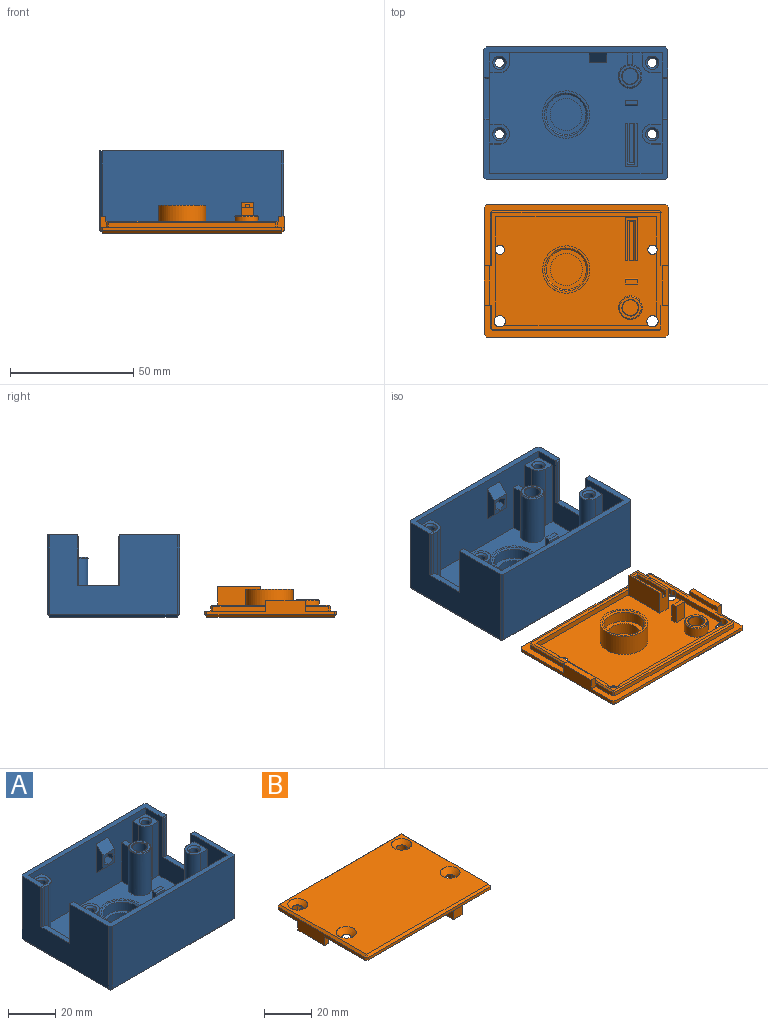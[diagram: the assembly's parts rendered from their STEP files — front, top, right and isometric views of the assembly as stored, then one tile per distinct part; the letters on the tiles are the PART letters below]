
ASSEMBLY  parts=2 mates=1
PART A: 120 faces, bbox 74.8x53.8x33.4 mm
  f0: plane 49x31mm, normal (-1,0,0), area 634.4mm2, adj f3,f4,f17,f19,f21,f23,f42,f43
  f1: plane 51.8x32.4mm, normal (1,0,0), area 1199.7mm2, adj f17,f21,f23,f81,f82,f83,f84,f85
  f2: plane 7x7mm, normal (0,-1,0), area 27.3mm2, adj f66,f67,f68,f69,f70,f71,f72,f73
  f3: plane 70x49mm, normal (0,0,1), area 2721.3mm2, adj f0,f4,f5,f16,f19,f25,f33,f34
  f4: plane 70x31mm, normal (0,-1,0), area 1569mm2, adj f0,f3,f16,f17,f33,f34,f35,f38
  f5: cylinder r=4.8mm len=21.6mm, axis (0,0,-1), area 602.9mm2, adj f3,f33,f34,f35,f113
  f6: plane 51.8x32.4mm, normal (-1,0,0), area 1325.7mm2, adj f17,f21,f22,f90,f94,f96,f103,f106
  f7: plane 72.8x32.4mm, normal (0,-1,0), area 2358.7mm2, adj f21,f87,f93,f96
  f8: cylinder r=1.9mm len=29.6mm, axis (0,0,1), area 353.4mm2, adj f13,f110
  f9: cylinder r=1.9mm len=29.6mm, axis (0,0,1), area 353.4mm2, adj f13,f111
  f10: cylinder r=1.9mm len=29.6mm, axis (0,0,1), area 353.4mm2, adj f13,f112
  f11: plane 72.8x32.4mm, normal (0,1,0), area 2358.7mm2, adj f17,f85,f89,f90
  f12: cylinder r=1.9mm len=29.6mm, axis (0,0,1), area 353.4mm2, adj f13,f109
  f13: plane 72.8x51.8mm, normal (0,0,-1), area 3725.7mm2, adj f8,f9,f10,f12,f88,f89,f93,f94
  f14: plane 19.9x1.2mm, normal (0,-1,0), area 23.9mm2, adj f23,f97,f98,f99
  f15: plane 19.9x1.2mm, normal (0,-1,0), area 23.9mm2, adj f22,f106,f107,f108
  f16: plane 49x31mm, normal (1,0,0), area 718.4mm2, adj f3,f4,f17,f19,f21,f22,f36,f39
  f17: plane 74.8x12.3mm, normal (0,0,1), area 226mm2, adj f0,f1,f4,f6,f11,f16,f85,f90
  f18: plane 19.9x1.2mm, normal (0,1,0), area 23.9mm2, adj f23,f100,f101,f102
  f19: plane 70x31mm, normal (0,1,0), area 2170mm2, adj f0,f3,f16,f21
  f20: plane 19.9x1.2mm, normal (0,1,0), area 23.9mm2, adj f22,f103,f104,f105
  f21: plane 74.8x24.3mm, normal (0,0,1), area 283.6mm2, adj f0,f1,f6,f7,f16,f19,f87,f96
  f22: plane 17.2x2.4mm, normal (0,0,1), area 39.1mm2, adj f6,f15,f16,f20,f103,f104,f106,f107
  f23: plane 17.2x2.4mm, normal (0,0,1), area 39.1mm2, adj f0,f1,f14,f18,f97,f98,f100,f101
  f24: cylinder r=8.15mm len=16.3mm, axis (0,0,-1), area 225.3mm2, adj f29,f115
  f25: cylinder r=9.6mm len=19.2mm, axis (0,0,-1), area 542.9mm2, adj f3,f26
  f26: plane 19.2x19.2mm, normal (0,0,1), area 49mm2, adj f25,f115
  f27: plane 13x13mm, normal (0,0,1), area 132.7mm2, adj f28
  f28: cylinder r=6.5mm len=13mm, axis (0,0,-1), area 204.2mm2, adj f27,f29
  f29: plane 16.3x16.3mm, normal (0,0,1), area 75.9mm2, adj f24,f28
  f30: cylinder r=3.2mm len=21.8mm, axis (0,0,-1), area 438.3mm2, adj f32,f114
  f31: plane 8.8x8.8mm, normal (0,0,1), area 24.5mm2, adj f113,f114
  f32: plane 6.4x6.4mm, normal (0,0,1), area 32.2mm2, adj f30
  f33: plane 20x4.85mm, normal (1,0,0), area 97mm2, adj f3,f4,f5,f35
  f34: plane 20x4.85mm, normal (-1,0,0), area 97mm2, adj f3,f4,f5,f35
  f35: plane 4.85x2.4mm, normal (0,0,1), area 11.4mm2, adj f4,f5,f33,f34
  f36: plane 28x4mm, normal (0,-1,0), area 112mm2, adj f3,f16,f37,f39
  f37: cylinder r=4mm len=28mm, axis (0,0,-1), area 175.9mm2, adj f3,f36,f38,f39
  f38: plane 28x4mm, normal (1,0,0), area 112mm2, adj f3,f4,f37,f39
  f39: plane 8x8mm, normal (0,0,1), area 37.7mm2, adj f4,f16,f36,f37,f38,f112
  f40: plane 28x4mm, normal (-1,0,0), area 112mm2, adj f3,f4,f41,f43
  f41: cylinder r=4mm len=28mm, axis (0,0,-1), area 175.9mm2, adj f3,f40,f42,f43
  f42: plane 28x4mm, normal (0,-1,0), area 112mm2, adj f0,f3,f41,f43
  f43: plane 8x8mm, normal (0,0,1), area 37.7mm2, adj f0,f4,f40,f41,f42,f111
  f44: plane 28x4mm, normal (0,1,0), area 112mm2, adj f3,f16,f46,f47
  f45: plane 28x4mm, normal (0,-1,0), area 112mm2, adj f3,f16,f46,f47
  f46: cylinder r=4mm len=28mm, axis (0,0,-1), area 351.9mm2, adj f3,f44,f45,f47
  f47: plane 8x8mm, normal (0,0,1), area 34.2mm2, adj f16,f44,f45,f46,f110
  f48: plane 28x4mm, normal (0,1,0), area 112mm2, adj f0,f3,f49,f51
  f49: cylinder r=4mm len=28mm, axis (0,0,-1), area 351.9mm2, adj f3,f48,f50,f51
  f50: plane 28x4mm, normal (0,-1,0), area 112mm2, adj f0,f3,f49,f51
  f51: plane 8x8mm, normal (0,0,1), area 34.2mm2, adj f0,f48,f49,f50,f109
  f52: plane 7x5mm, normal (0,1,0), area 29.2mm2, adj f3,f53,f54,f56,f57,f59,f60,f116
  f53: plane 16x1.8mm, normal (0,0,1), area 28.8mm2, adj f52,f54,f55,f56
  f54: plane 16x2.4mm, normal (1,0,0), area 38.4mm2, adj f52,f53,f55,f116
  f55: plane 2.4x1.8mm, normal (0,1,0), area 4.3mm2, adj f53,f54,f56,f118
  f56: plane 16x2.4mm, normal (-1,0,0), area 38.4mm2, adj f52,f53,f55,f117
  f57: plane 17.6x7mm, normal (-1,0,0), area 123.2mm2, adj f3,f52,f58,f60
  f58: plane 7x5mm, normal (0,-1,0), area 35mm2, adj f3,f57,f59,f60
  f59: plane 17.6x7mm, normal (1,0,0), area 123.2mm2, adj f3,f52,f58,f60
  f60: plane 17.6x5mm, normal (0,0,1), area 38.2mm2, adj f52,f57,f58,f59,f116,f117,f118
  f61: plane 5x2.4mm, normal (-1,0,0), area 11.8mm2, adj f3,f62,f64,f65,f119
  f62: plane 5x4.4mm, normal (0,-1,0), area 22mm2, adj f3,f61,f63,f119
  f63: plane 5x2.4mm, normal (1,0,0), area 11.8mm2, adj f3,f62,f64,f65,f119
  f64: plane 5x5mm, normal (0,1,0), area 25mm2, adj f3,f61,f63,f65
  f65: plane 5x1.8mm, normal (0,0,1), area 9mm2, adj f61,f63,f64,f119
  f66: plane 15x4mm, normal (1,0,0), area 44mm2, adj f2,f4,f68,f69
  f67: plane 15x4mm, normal (-1,0,0), area 44mm2, adj f2,f4,f68,f69
  f68: plane 7x4mm, normal (0,-0.71,0.71), area 39.6mm2, adj f2,f4,f66,f67
  f69: plane 7x4mm, normal (0,-0.71,-0.71), area 39.6mm2, adj f2,f4,f66,f67
  f70: plane 4x2.5mm, normal (0.5,0,0.87), area 11.5mm2, adj f2,f71,f75,f76
  f71: plane 4x2.5mm, normal (-0.5,0,0.87), area 11.5mm2, adj f2,f70,f72,f76
  f72: plane 4x2.89mm, normal (-1,0,0), area 11.5mm2, adj f2,f71,f73,f76
  f73: plane 4x2.5mm, normal (-0.5,0,-0.87), area 11.5mm2, adj f2,f72,f74,f76
  f74: plane 4x2.5mm, normal (0.5,0,-0.87), area 11.5mm2, adj f2,f73,f75,f76
  f75: plane 4x2.89mm, normal (1,0,0), area 11.5mm2, adj f2,f70,f74,f76
  f76: plane 5.77x5mm, normal (0,-1,0), area 21.7mm2, adj f70,f71,f72,f73,f74,f75
  f77: plane 7x1.4mm, normal (0,0,-1), area 9.8mm2, adj f0,f78,f80,f84
  f78: plane 12x1.4mm, normal (0,1,0), area 16.8mm2, adj f0,f77,f79,f83
  f79: plane 7x1.4mm, normal (0,0,1), area 9.8mm2, adj f0,f78,f80,f81
  f80: plane 12x1.4mm, normal (0,-1,0), area 16.8mm2, adj f0,f77,f79,f82
  f81: plane 9x1mm, normal (0.71,0,0.71), area 11.3mm2, adj f1,f79,f82,f83
  f82: plane 14x1mm, normal (0.71,-0.71,0), area 18.4mm2, adj f1,f80,f81,f84
  f83: plane 14x1mm, normal (0.71,0.71,0), area 18.4mm2, adj f1,f78,f81,f84
  f84: plane 9x1mm, normal (0.71,0,-0.71), area 11.3mm2, adj f1,f77,f82,f83
  f85: plane 32.4x1mm, normal (0.71,0.71,0), area 45.8mm2, adj f1,f11,f17,f86
  f86: plane 1x1mm, normal (0.58,0.58,-0.58), area 0.9mm2, adj f85,f88,f89
  f87: plane 32.4x1mm, normal (0.71,-0.71,0), area 45.8mm2, adj f1,f7,f21,f91
  f88: plane 51.8x1mm, normal (0.71,0,-0.71), area 73.3mm2, adj f1,f13,f86,f91
  f89: plane 72.8x1mm, normal (0,0.71,-0.71), area 103mm2, adj f11,f13,f86,f92
  f90: plane 32.4x1mm, normal (-0.71,0.71,0), area 45.8mm2, adj f6,f11,f17,f92
  f91: plane 1x1mm, normal (0.58,-0.58,-0.58), area 0.9mm2, adj f87,f88,f93
  f92: plane 1x1mm, normal (-0.58,0.58,-0.58), area 0.9mm2, adj f89,f90,f94
  f93: plane 72.8x1mm, normal (0,-0.71,-0.71), area 103mm2, adj f7,f13,f91,f95
  f94: plane 51.8x1mm, normal (-0.71,0,-0.71), area 73.3mm2, adj f6,f13,f92,f95
  f95: plane 1x1mm, normal (-0.58,-0.58,-0.58), area 0.9mm2, adj f93,f94,f96
  f96: plane 32.4x1mm, normal (-0.71,-0.71,0), area 45.8mm2, adj f6,f7,f21,f95
  f97: plane 20.5x0.6mm, normal (0.71,-0.71,0), area 17.1mm2, adj f1,f14,f23,f99
  f98: plane 20.5x0.6mm, normal (-0.71,-0.71,0), area 17.1mm2, adj f0,f14,f23,f99
  f99: plane 2.4x0.6mm, normal (0,-0.71,0.71), area 1.5mm2, adj f14,f17,f97,f98
  f100: plane 20.5x0.6mm, normal (0.71,0.71,0), area 17.1mm2, adj f1,f18,f23,f102
  f101: plane 20.5x0.6mm, normal (-0.71,0.71,0), area 17.1mm2, adj f0,f18,f23,f102
  f102: plane 2.4x0.6mm, normal (0,0.71,0.71), area 1.5mm2, adj f18,f21,f100,f101
  f103: plane 20.5x0.6mm, normal (-0.71,0.71,0), area 17.1mm2, adj f6,f20,f22,f105
  f104: plane 20.5x0.6mm, normal (0.71,0.71,0), area 17.1mm2, adj f16,f20,f22,f105
  f105: plane 2.4x0.6mm, normal (0,0.71,0.71), area 1.5mm2, adj f20,f21,f103,f104
  f106: plane 20.5x0.6mm, normal (-0.71,-0.71,0), area 17.1mm2, adj f6,f15,f22,f108
  f107: plane 20.5x0.6mm, normal (0.71,-0.71,0), area 17.1mm2, adj f15,f16,f22,f108
  f108: plane 2.4x0.6mm, normal (0,-0.71,0.71), area 1.5mm2, adj f15,f17,f106,f107
  f109: cone r=1.9mm half-angle=45deg, axis (0,0,1), area 16.3mm2, adj f12,f51
  f110: cone r=1.9mm half-angle=45deg, axis (0,0,1), area 16.3mm2, adj f8,f47
  f111: cone r=1.9mm half-angle=45deg, axis (0,0,1), area 16.3mm2, adj f9,f43
  f112: cone r=1.9mm half-angle=45deg, axis (0,0,1), area 16.3mm2, adj f10,f39
  f113: cone r=4.4mm half-angle=45deg, axis (0,0,-1), area 16.3mm2, adj f5,f31
  f114: cone r=3mm half-angle=45deg, axis (0,0,1), area 5.9mm2, adj f30,f31
  f115: cone r=8.15mm half-angle=45deg, axis (0,0,1), area 45.1mm2, adj f24,f26
  f116: plane 16.6x0.6mm, normal (0.71,0,0.71), area 13.8mm2, adj f52,f54,f60,f118
  f117: plane 16.6x0.6mm, normal (-0.71,0,0.71), area 13.8mm2, adj f52,f56,f60,f118
  f118: plane 3x0.6mm, normal (0,0.71,0.71), area 2mm2, adj f55,f60,f116,f117
  f119: plane 5x0.6mm, normal (0,-0.71,0.71), area 4.2mm2, adj f61,f62,f63,f65
PART B: 90 faces, bbox 74.8x53.8x12.4 mm
  f0: plane 65.2x44.2mm, normal (0,0,-1), area 2371.2mm2, adj f6,f7,f8,f9,f13,f19,f22,f24
  f1: plane 74.8x12.9mm, normal (0,0,-1), area 247.7mm2, adj f3,f4,f10,f36,f40,f48,f51,f52
  f2: plane 74.8x24.9mm, normal (0,0,-1), area 310.1mm2, adj f4,f5,f10,f38,f41,f49,f50,f59
  f3: plane 72.8x1.4mm, normal (0,1,0), area 101.9mm2, adj f1,f61,f65,f66
  f4: plane 51.8x5.9mm, normal (-1,0,0), area 144.5mm2, adj f1,f2,f40,f41,f43,f61,f63,f64
  f5: plane 72.8x1.4mm, normal (0,-1,0), area 101.9mm2, adj f2,f63,f69,f72
  f6: cylinder r=1.9mm len=3.8mm, axis (0,0,-1), area 6.4mm2, adj f0,f45,f57,f58,f60
  f7: cylinder r=2.3mm len=4.6mm, axis (0,0,-1), area 24.7mm2, adj f0,f47,f53,f58,f60
  f8: cylinder r=1.9mm len=3.8mm, axis (0,0,-1), area 6.4mm2, adj f0,f44,f54,f55,f60
  f9: cylinder r=2.3mm len=4.6mm, axis (0,0,-1), area 24.7mm2, adj f0,f46,f53,f54,f60
  f10: plane 51.8x5.9mm, normal (1,0,0), area 144.5mm2, adj f1,f2,f36,f38,f39,f66,f70,f72
  f11: plane 72.8x51.8mm, normal (0,0,1), area 3549.4mm2, adj f44,f45,f46,f47,f64,f65,f69,f70
  f12: cylinder r=8.15mm len=16.3mm, axis (0,0,1), area 225.3mm2, adj f17,f79
  f13: cylinder r=9.6mm len=19.2mm, axis (0,0,1), area 542.9mm2, adj f0,f14
  f14: plane 19.2x19.2mm, normal (0,0,-1), area 49mm2, adj f13,f79
  f15: plane 13x13mm, normal (0,0,-1), area 132.7mm2, adj f16
  f16: cylinder r=6.5mm len=13mm, axis (0,0,1), area 204.2mm2, adj f15,f17
  f17: plane 16.3x16.3mm, normal (0,0,-1), area 75.9mm2, adj f12,f16
  f18: cylinder r=3.2mm len=6.4mm, axis (0,0,1), area 88.5mm2, adj f21,f74
  f19: cylinder r=4.8mm len=9.6mm, axis (0,0,1), area 126.7mm2, adj f0,f73
  f20: plane 8.8x8.8mm, normal (0,0,-1), area 24.5mm2, adj f73,f74
  f21: plane 6.4x6.4mm, normal (0,0,-1), area 32.2mm2, adj f18
  f22: plane 10x5mm, normal (0,1,0), area 43.9mm2, adj f0,f23,f29,f31,f32,f34,f35,f81
  f23: plane 16x1.8mm, normal (0,0,-1), area 28.8mm2, adj f22,f29,f30,f31
  f24: plane 8x2.4mm, normal (-1,0,0), area 19mm2, adj f0,f25,f27,f28,f80
  f25: plane 7.4x5mm, normal (0,-1,0), area 37mm2, adj f0,f24,f26,f80
  f26: plane 8x2.4mm, normal (1,0,0), area 19mm2, adj f0,f25,f27,f28,f80
  f27: plane 8x5mm, normal (0,1,0), area 40mm2, adj f0,f24,f26,f28
  f28: plane 5x1.8mm, normal (0,0,-1), area 9mm2, adj f24,f26,f27,f80
  f29: plane 16x2.6mm, normal (1,0,0), area 41.6mm2, adj f22,f23,f30,f81
  f30: plane 2.6x1.8mm, normal (0,1,0), area 4.7mm2, adj f23,f29,f31,f83
  f31: plane 16x2.6mm, normal (-1,0,0), area 41.6mm2, adj f22,f23,f30,f82
  f32: plane 17.6x10mm, normal (-1,0,0), area 176mm2, adj f0,f22,f33,f35
  f33: plane 10x5mm, normal (0,-1,0), area 50mm2, adj f0,f32,f34,f35
  f34: plane 17.6x10mm, normal (1,0,0), area 176mm2, adj f0,f22,f33,f35
  f35: plane 17.6x5mm, normal (0,0,-1), area 38.2mm2, adj f22,f32,f33,f34,f81,f82,f83
  f36: plane 4.5x3.2mm, normal (0,1,0), area 11.5mm2, adj f1,f10,f37,f39,f48,f60,f86
  f37: plane 16x2.1mm, normal (-1,0,0), area 33.6mm2, adj f36,f38,f39,f60
  f38: plane 4.5x3.2mm, normal (0,-1,0), area 11.5mm2, adj f2,f10,f37,f39,f50,f60,f89
  f39: plane 16x2.4mm, normal (0,0,-1), area 38.4mm2, adj f10,f36,f37,f38
  f40: plane 4.5x3.2mm, normal (0,1,0), area 11.5mm2, adj f1,f4,f42,f43,f52,f60,f84
  f41: plane 4.5x3.2mm, normal (0,-1,0), area 11.5mm2, adj f2,f4,f42,f43,f49,f60,f87
  f42: plane 16x2.1mm, normal (1,0,0), area 33.6mm2, adj f40,f41,f43,f60
  f43: plane 16x2.4mm, normal (0,0,-1), area 38.4mm2, adj f4,f40,f41,f42
  f44: cone r=1.9mm half-angle=45deg, axis (0,0,1), area 62.3mm2, adj f8,f11
  f45: cone r=1.9mm half-angle=45deg, axis (0,0,1), area 62.3mm2, adj f6,f11
  f46: cone r=1.9mm half-angle=45deg, axis (0,0,1), area 54.9mm2, adj f9,f11
  f47: cone r=1.9mm half-angle=45deg, axis (0,0,1), area 54.9mm2, adj f7,f11
  f48: plane 9.5x1.8mm, normal (1,0,0), area 17.1mm2, adj f1,f36,f75,f86
  f49: plane 21.5x1.8mm, normal (-1,0,0), area 38.7mm2, adj f2,f41,f77,f87
  f50: plane 21.5x1.8mm, normal (1,0,0), area 38.7mm2, adj f2,f38,f78,f89
  f51: plane 68x1.8mm, normal (0,1,0), area 122.4mm2, adj f1,f75,f76,f85
  f52: plane 9.5x1.8mm, normal (-1,0,0), area 17.1mm2, adj f1,f40,f76,f84
  f53: plane 58.7x2.4mm, normal (0,-1,0), area 140.9mm2, adj f0,f7,f9,f60
  f54: plane 26.32x2.4mm, normal (-1,0,0), area 63.2mm2, adj f0,f8,f9,f60
  f55: plane 12.58x2.4mm, normal (-1,0,0), area 30.2mm2, adj f0,f8,f56,f60
  f56: plane 65.2x2.4mm, normal (0,1,0), area 156.5mm2, adj f0,f55,f57,f60
  f57: plane 12.58x2.4mm, normal (1,0,0), area 30.2mm2, adj f0,f6,f56,f60
  f58: plane 26.32x2.4mm, normal (1,0,0), area 63.2mm2, adj f0,f6,f7,f60
  f59: plane 68x1.8mm, normal (0,-1,0), area 122.4mm2, adj f2,f77,f78,f88
  f60: plane 70x47.4mm, normal (0,0,-1), area 378.7mm2, adj f6,f7,f8,f9,f36,f37,f38,f40
  f61: plane 1.4x1mm, normal (-0.71,0.71,0), area 2mm2, adj f1,f3,f4,f62
  f62: plane 1x1mm, normal (-0.58,0.58,0.58), area 0.9mm2, adj f61,f64,f65
  f63: plane 1.4x1mm, normal (-0.71,-0.71,0), area 2mm2, adj f2,f4,f5,f67
  f64: plane 51.8x1mm, normal (-0.71,0,0.71), area 73.3mm2, adj f4,f11,f62,f67
  f65: plane 72.8x1mm, normal (0,0.71,0.71), area 103mm2, adj f3,f11,f62,f68
  f66: plane 1.4x1mm, normal (0.71,0.71,0), area 2mm2, adj f1,f3,f10,f68
  f67: plane 1x1mm, normal (-0.58,-0.58,0.58), area 0.9mm2, adj f63,f64,f69
  f68: plane 1x1mm, normal (0.58,0.58,0.58), area 0.9mm2, adj f65,f66,f70
  f69: plane 72.8x1mm, normal (0,-0.71,0.71), area 103mm2, adj f5,f11,f67,f71
  f70: plane 51.8x1mm, normal (0.71,0,0.71), area 73.3mm2, adj f10,f11,f68,f71
  f71: plane 1x1mm, normal (0.58,-0.58,0.58), area 0.9mm2, adj f69,f70,f72
  f72: plane 1.4x1mm, normal (0.71,-0.71,0), area 2mm2, adj f2,f5,f10,f71
  f73: cone r=4.8mm half-angle=45deg, axis (0,0,1), area 16.3mm2, adj f19,f20
  f74: cone r=3.4mm half-angle=45deg, axis (0,0,-1), area 5.9mm2, adj f18,f20
  f75: plane 2.2x0.8mm, normal (0.71,0.71,0), area 2.3mm2, adj f1,f48,f51,f85,f86
  f76: plane 2.2x0.8mm, normal (-0.71,0.71,0), area 2.3mm2, adj f1,f51,f52,f84,f85
  f77: plane 2.2x0.8mm, normal (-0.71,-0.71,0), area 2.3mm2, adj f2,f49,f59,f87,f88
  f78: plane 2.2x0.8mm, normal (0.71,-0.71,0), area 2.3mm2, adj f2,f50,f59,f88,f89
  f79: cone r=8.75mm half-angle=45deg, axis (0,0,-1), area 45.1mm2, adj f12,f14
  f80: plane 5x0.6mm, normal (0,-0.71,-0.71), area 4.2mm2, adj f24,f25,f26,f28
  f81: plane 16.6x0.6mm, normal (0.71,0,-0.71), area 13.8mm2, adj f22,f29,f35,f83
  f82: plane 16.6x0.6mm, normal (-0.71,0,-0.71), area 13.8mm2, adj f22,f31,f35,f83
  f83: plane 3x0.6mm, normal (0,0.71,-0.71), area 2mm2, adj f30,f35,f81,f82
  f84: plane 9.9x0.6mm, normal (-0.71,0,-0.71), area 8.3mm2, adj f40,f52,f60,f76,f85
  f85: plane 68.8x0.6mm, normal (0,0.71,-0.71), area 58.1mm2, adj f51,f60,f75,f76,f84,f86
  f86: plane 9.9x0.6mm, normal (0.71,0,-0.71), area 8.3mm2, adj f36,f48,f60,f75,f85
  f87: plane 21.9x0.6mm, normal (-0.71,0,-0.71), area 18.4mm2, adj f41,f49,f60,f77,f88
  f88: plane 68.8x0.6mm, normal (0,-0.71,-0.71), area 58.1mm2, adj f59,f60,f77,f78,f87,f89
  f89: plane 21.9x0.6mm, normal (0.71,0,-0.71), area 18.4mm2, adj f38,f50,f60,f78,f88
PLACE A t=(-1.56,30.97,3.73)mm
PLACE B rot(axis=(1,0,0),180deg) t=(-1.44,-31.97,63.73)mm
MATE planar A.f13 <-> B.f11  axis (0,0,-1) through (1.09,31.4,1.33)mm
